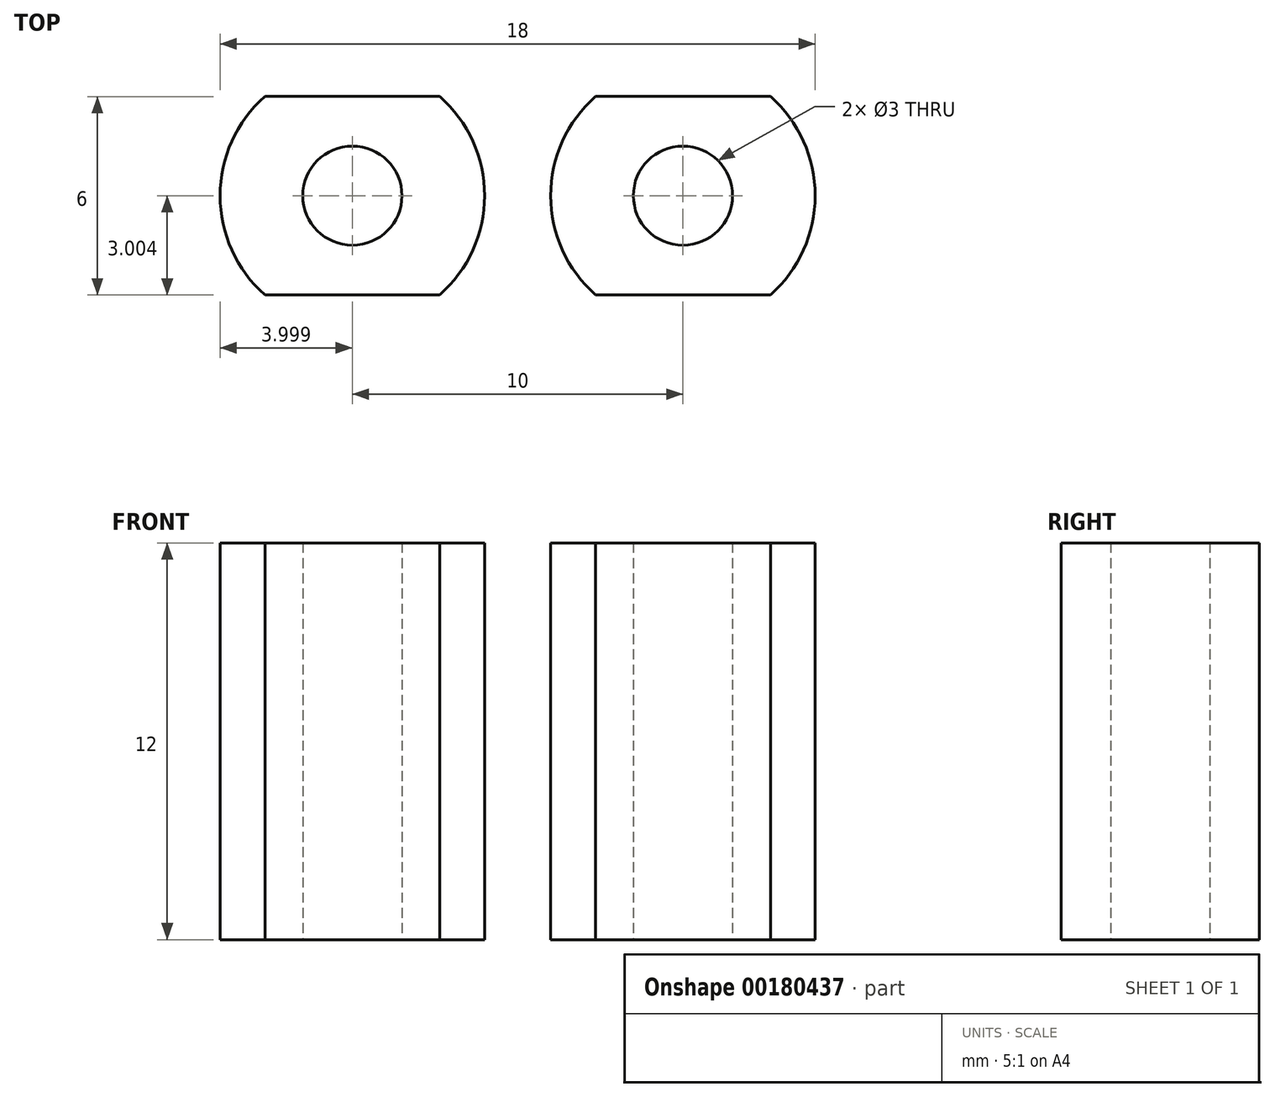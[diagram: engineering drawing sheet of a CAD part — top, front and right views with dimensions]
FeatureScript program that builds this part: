
annotation { "Feature Type Name" : "Feature", "Feature Type Description" : "" }
export const myFeature = defineFeature(function(context is Context, id is Id, definition is map)
    precondition{}
    {
        {
            var Q0;
            Q0=qCreatedBy(makeId("Top.planeOp"),FACE);
            var sketch = newSketch(context, id + "F0", { "sketchPlane" : qUnion([Q0])});
            skCircle(sketch, "E0", {"center": v(-45.11, 21.51) * mm, "radius": 1.5 * mm});
            skCircle(sketch, "E1", {"center": v(-45.11, 21.51) * mm, "radius": 4 * mm});
            skLineSegment(sketch, "E2.bottom", {"start": v(-41.11, 24.51) * mm, "end": v(-49.11, 24.51) * mm});
            skLineSegment(sketch, "E2.top", {"start": v(-41.11, 18.51) * mm, "end": v(-49.11, 18.51) * mm});
            skLineSegment(sketch, "E2.left", {"start": v(-41.11, 24.51) * mm, "end": v(-41.11, 18.51) * mm});
            skLineSegment(sketch, "E2.right", {"start": v(-49.11, 24.51) * mm, "end": v(-49.11, 18.51) * mm});
            skSolve(sketch);
        }
        {
            var Q0;
            Q0=makeQuery(id+"F0.imprint","IMPRINT",FACE,{"disambiguationData":[TD([[makeQuery(id+"F0.imprint","IMPRINT",EDGE,{"derivedFrom":sQuery(id+"F0.wireOp",EDGE,"E0")}),-1.0]])]});
            extrude(context, id + "F1", {"entities" : qUnion([Q0]), "depth" : 12 * mm});
        }
        {
            var Q0;
            Q0=makeQuery(id+"F1.opExtrude","SWEPT_BODY",BODY,{"disambiguationData":[OSD([sQuery(id+"F0.wireOp",EDGE,"E0"),sQuery(id+"F0.wireOp",EDGE,"E1"),sQuery(id+"F0.wireOp",EDGE,"E2.bottom"),sQuery(id+"F0.wireOp",EDGE,"E2.top")])]});
            transform(context, id + "F2", {"entities" : qUnion([Q0]), "transformType" : TransformType.TRANSLATION_3D, "dx" : 10 * mm, "dy" : 0 * mm, "dz" : 0 * mm, "makeCopy" : true});
        }
    });
